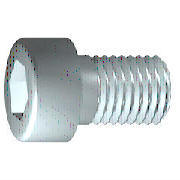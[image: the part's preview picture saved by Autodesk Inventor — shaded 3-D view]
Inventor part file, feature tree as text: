
AUTODESK INVENTOR PART (.ipt)
format: ipt  version: 2022 (Build 260153000, 153)  size: 197,120 bytes
history: native  units: mm (DEFAULTED — no unit token found)
features: sketch x2, other x1, extrude x1, plane x1, fillet x1
ambient origin geometry x7: Origin, YZ Plane, XY Plane, X Axis, Y Axis, Z Axis, Center Point
bodies: Solid1 (feature_tree)
feature tree (6):
  other  "Cuerpo"
  extrude  "Ranura"  Depth=6.0mm
  plane  "Work Plane1"
  fillet  "Fillet2"  Radius=6.0mm
  sketch  "Boceto1"  dims[d1=9.5mm d2=0.61355mm d3=6.0mm]
  sketch  "Boceto2"  dims[d4=3.0mm d5=60.0deg d6=6.0mm d7=6.0mm d8=5.773503mm d9=10.0mm d10=90.0deg d11=10.0mm d12=0.0mm d13=9.5mm d14=0.0mm d15=0.61345mm d16=0.61345mm d17=0.6mm d19=0.0mm d26=12.0mm d27=45.0deg d28=0.0mm d29=0.0mm d30=0.1mm]
